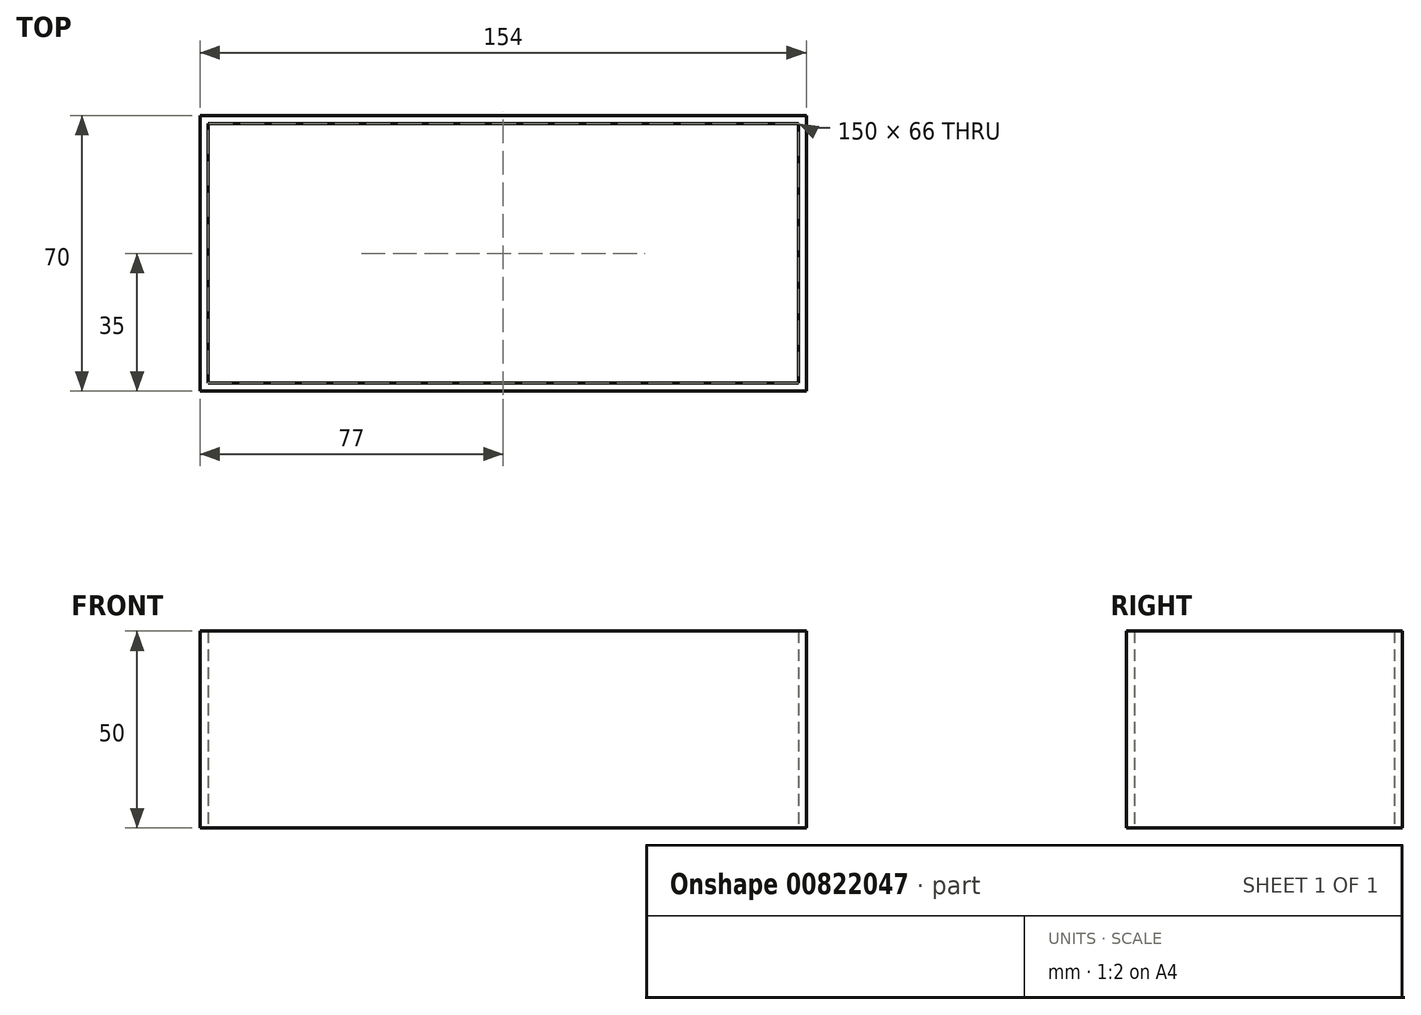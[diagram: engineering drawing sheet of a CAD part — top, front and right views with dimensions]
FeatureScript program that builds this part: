
annotation { "Feature Type Name" : "Feature", "Feature Type Description" : "" }
export const myFeature = defineFeature(function(context is Context, id is Id, definition is map)
    precondition{}
    {
        {
            var Q0;
            Q0=qCreatedBy(makeId("Top.planeOp"),FACE);
            var sketch = newSketch(context, id + "F0", { "sketchPlane" : qUnion([Q0])});
            skLineSegment(sketch, "E0", {"start": v(-75, 0) * mm, "end": v(-75, -33) * mm});
            skLineSegment(sketch, "E1.MirrorCS", {"start": v(75, 0) * mm, "end": v(75, -33) * mm});
            skLineSegment(sketch, "E2", {"start": v(-75, -33) * mm, "end": v(75, -33) * mm});
            skLineSegment(sketch, "E3.0", {"start": v(77, 0) * mm, "end": v(77, -35) * mm});
            skLineSegment(sketch, "E3.1", {"start": v(-77, -35) * mm, "end": v(77, -35) * mm});
            skLineSegment(sketch, "E3.2", {"start": v(-77, 0) * mm, "end": v(-77, -35) * mm});
            skLineSegment(sketch, "E4", {"start": v(-75, 0) * mm, "end": v(-77, 0) * mm});
            skLineSegment(sketch, "E5", {"start": v(77, 0) * mm, "end": v(75, 0) * mm});
            skLineSegment(sketch, "E6.MirrorCS", {"start": v(-75, 0) * mm, "end": v(-75, 33) * mm});
            skLineSegment(sketch, "E7.MirrorCS", {"start": v(75, 0) * mm, "end": v(75, 33) * mm});
            skLineSegment(sketch, "E8.MirrorCS", {"start": v(77, 0) * mm, "end": v(77, 35) * mm});
            skLineSegment(sketch, "E9.MirrorCS", {"start": v(-77, 0) * mm, "end": v(-77, 35) * mm});
            skLineSegment(sketch, "E10.MirrorCS", {"start": v(-77, 35) * mm, "end": v(77, 35) * mm});
            skLineSegment(sketch, "E11.MirrorCS", {"start": v(-75, 33) * mm, "end": v(75, 33) * mm});
            skSolve(sketch);
        }
        {
            var Q0;
            Q0 = qSketchRegion(id + "F0", true);
            extrude(context, id + "F1", {"entities" : qUnion([Q0]), "depth" : 50 * mm, "offsetDistance" : 25 * mm, "symmetric" : true});
        }
    });
